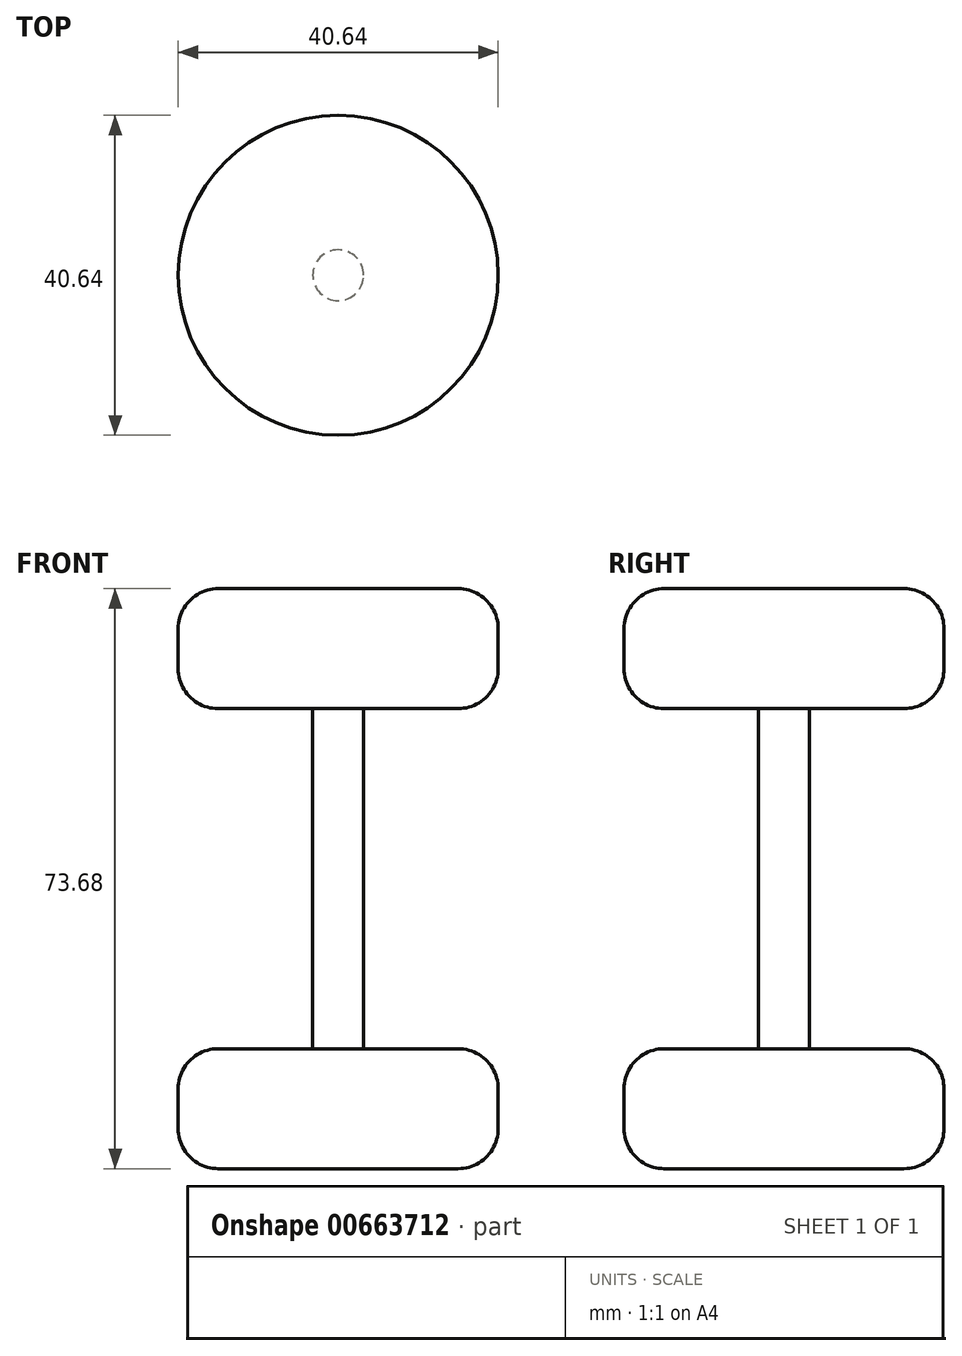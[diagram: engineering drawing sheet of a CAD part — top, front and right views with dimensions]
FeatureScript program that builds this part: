
annotation { "Feature Type Name" : "Feature", "Feature Type Description" : "" }
export const myFeature = defineFeature(function(context is Context, id is Id, definition is map)
    precondition{}
    {
        {
            var Q0;
            Q0=qCreatedBy(makeId("Front.planeOp"),FACE);
            var sketch = newSketch(context, id + "F0", { "sketchPlane" : qUnion([Q0])});
            skLineSegment(sketch, "E0", {"start": v(0, -38.8) * mm, "end": v(0, 34.87) * mm});
            skLineSegment(sketch, "E1.bottom", {"start": v(0, 34.87) * mm, "end": v(20.32, 34.87) * mm});
            skLineSegment(sketch, "E1.top", {"start": v(0, 19.63) * mm, "end": v(20.32, 19.63) * mm});
            skLineSegment(sketch, "E1.left", {"start": v(0, 34.87) * mm, "end": v(0, 19.63) * mm});
            skLineSegment(sketch, "E1.right", {"start": v(20.32, 34.87) * mm, "end": v(20.32, 19.63) * mm});
            skLineSegment(sketch, "E2.bottom", {"start": v(0, -38.8) * mm, "end": v(20.32, -38.8) * mm});
            skLineSegment(sketch, "E2.top", {"start": v(0, -23.57) * mm, "end": v(20.32, -23.57) * mm});
            skLineSegment(sketch, "E2.left", {"start": v(0, -38.8) * mm, "end": v(0, -23.57) * mm});
            skLineSegment(sketch, "E2.right", {"start": v(20.32, -38.8) * mm, "end": v(20.32, -23.57) * mm});
            skLineSegment(sketch, "E3", {"start": v(3.23, 19.63) * mm, "end": v(3.23, -23.57) * mm});
            skSolve(sketch);
        }
        {
            var Q0;
            Q0 = qSketchRegion(id + "F0", true);
            var Q1;
            Q1=sQuery(id+"F0.wireOp",EDGE,"E0");
            revolve(context, id + "F1", {"entities" : qUnion([Q0]), "axis" : qUnion([Q1]), "revolveType" : RevolveType.FULL});
        }
        {
            var Q0;
            Q0=makeQuery(id+"F1.opRevolve","SWEPT_EDGE",EDGE,{"disambiguationData":[OSD([sQuery(id+"F0.wireOp",EDGE,"E1.bottom"),sQuery(id+"F0.wireOp",EDGE,"E1.right")])]});
            var Q1;
            Q1=makeQuery(id+"F1.opRevolve","SWEPT_EDGE",EDGE,{"disambiguationData":[OSD([sQuery(id+"F0.wireOp",EDGE,"E1.top"),sQuery(id+"F0.wireOp",EDGE,"E1.right")])]});
            var Q2;
            Q2=makeQuery(id+"F1.opRevolve","SWEPT_EDGE",EDGE,{"disambiguationData":[OSD([sQuery(id+"F0.wireOp",EDGE,"E2.top"),sQuery(id+"F0.wireOp",EDGE,"E2.right")])]});
            var Q3;
            Q3=makeQuery(id+"F1.opRevolve","SWEPT_EDGE",EDGE,{"disambiguationData":[OSD([sQuery(id+"F0.wireOp",EDGE,"E2.bottom"),sQuery(id+"F0.wireOp",EDGE,"E2.right")])]});
            fillet(context, id + "F2", {"entities" : qUnion([Q0, Q1, Q2, Q3]), "radius" : 5.08 * mm, "tangentPropagation" : true, "allowEdgeOverflow" : false});
        }
    });
